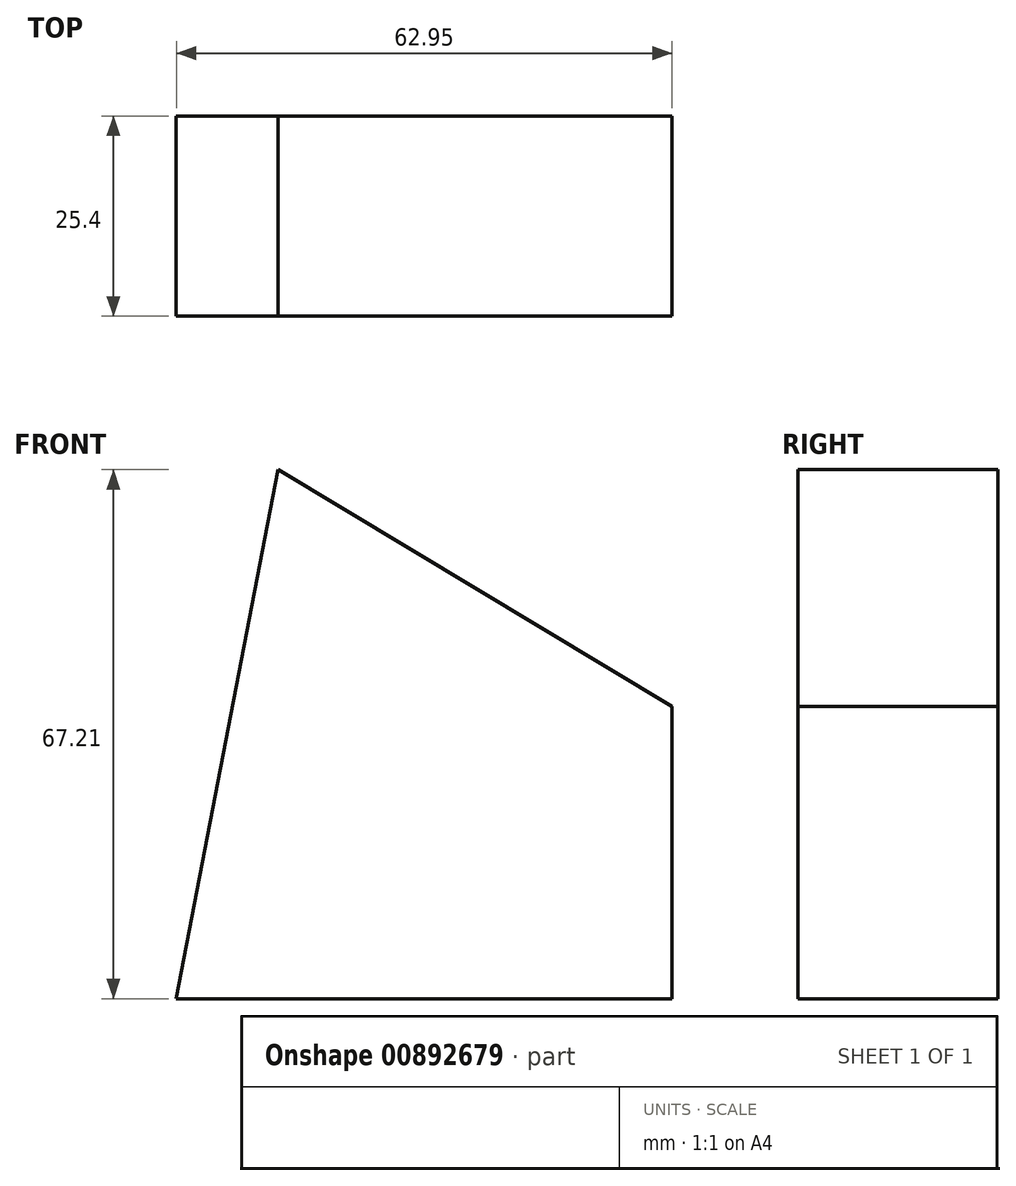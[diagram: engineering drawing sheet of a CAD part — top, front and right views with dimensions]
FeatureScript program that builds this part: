
annotation { "Feature Type Name" : "Feature", "Feature Type Description" : "" }
export const myFeature = defineFeature(function(context is Context, id is Id, definition is map)
    precondition{}
    {
        {
            var Q0;
            Q0=qCreatedBy(makeId("Front.planeOp"),FACE);
            var sketch = newSketch(context, id + "F0", { "sketchPlane" : qUnion([Q0])});
            skLineSegment(sketch, "E0", {"start": v(41.1, 8.7) * mm, "end": v(41.1, -28.42) * mm});
            skLineSegment(sketch, "E1", {"start": v(41.1, -28.42) * mm, "end": v(-21.86, -28.42) * mm});
            skLineSegment(sketch, "E2", {"start": v(-21.86, -28.42) * mm, "end": v(-8.97, 38.79) * mm});
            skLineSegment(sketch, "E3", {"start": v(-8.97, 38.79) * mm, "end": v(41.1, 8.7) * mm});
            skSolve(sketch);
        }
        {
            var Q0;
            Q0=makeQuery(id+"F0.imprint","IMPRINT",FACE,{"disambiguationData":[TD([[makeQuery(id+"F0.imprint","IMPRINT",EDGE,{"derivedFrom":sQuery(id+"F0.wireOp",EDGE,"E0")}),-1.0]])]});
            extrude(context, id + "F1", {"entities" : qUnion([Q0]), "depth" : 25.4 * mm, "offsetDistance" : 25.4 * mm});
        }
    });
